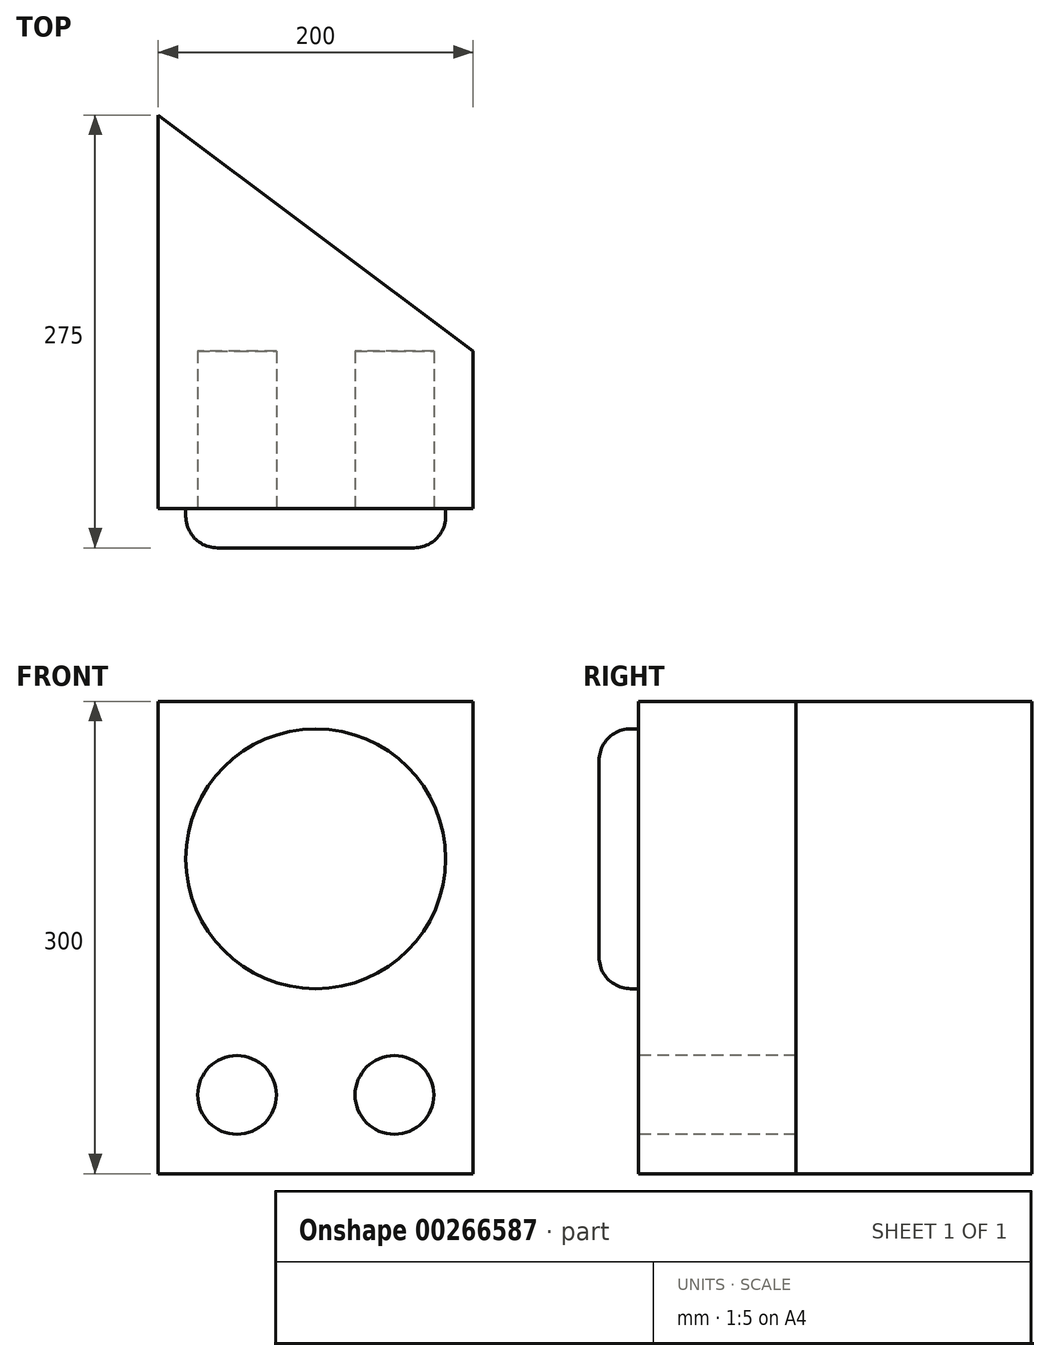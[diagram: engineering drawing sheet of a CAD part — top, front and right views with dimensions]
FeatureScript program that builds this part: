
annotation { "Feature Type Name" : "Feature", "Feature Type Description" : "" }
export const myFeature = defineFeature(function(context is Context, id is Id, definition is map)
    precondition{}
    {
        {
            var Q0;
            Q0=qCreatedBy(makeId("Front.planeOp"),FACE);
            var sketch = newSketch(context, id + "F0", { "sketchPlane" : qUnion([Q0])});
            skLineSegment(sketch, "E0.bottom", {"start": v(0, 0) * mm, "end": v(200, 0) * mm});
            skLineSegment(sketch, "E0.top", {"start": v(0, 300) * mm, "end": v(200, 300) * mm});
            skLineSegment(sketch, "E0.left", {"start": v(0, 0) * mm, "end": v(0, 300) * mm});
            skLineSegment(sketch, "E0.right", {"start": v(200, 0) * mm, "end": v(200, 300) * mm});
            skSolve(sketch);
        }
        {
            var Q0;
            Q0=makeQuery(id+"F0.imprint","IMPRINT",FACE,{"disambiguationData":[TD([[makeQuery(id+"F0.imprint","IMPRINT",EDGE,{"derivedFrom":sQuery(id+"F0.wireOp",EDGE,"E0.bottom")}),1.0]])]});
            extrude(context, id + "F1", {"entities" : qUnion([Q0]), "oppositeDirection" : true, "depth" : 250 * mm});
        }
        {
            var Q0;
            Q0=makeQuery(id+"F1.opExtrude","CAP_FACE",FACE,{"disambiguationData":[OSD([sQuery(id+"F0.wireOp",EDGE,"E0.bottom"),sQuery(id+"F0.wireOp",EDGE,"E0.top"),sQuery(id+"F0.wireOp",EDGE,"E0.left"),sQuery(id+"F0.wireOp",EDGE,"E0.right")])],"isStart":true});
            var sketch = newSketch(context, id + "F2", { "sketchPlane" : qUnion([Q0])});
            skCircle(sketch, "E1", {"center": v(100, 200) * mm, "radius": 82.5 * mm});
            skPoint(sketch, "E1.centerSnap0", {"position": v(100, 300) * mm});
            skSolve(sketch);
        }
        {
            var Q0;
            Q0=makeQuery(id+"F2.imprint","IMPRINT",FACE,{"disambiguationData":[TD([[makeQuery(id+"F2.imprint","IMPRINT",EDGE,{"derivedFrom":sQuery(id+"F2.wireOp",EDGE,"E1")}),1.0]])]});
            extrude(context, id + "F3", {"entities" : qUnion([Q0]), "operationType" : NewBodyOperationType.ADD, "depth" : 25 * mm});
        }
        {
            var Q0;
            Q0=makeQuery(id+"F1.opExtrude","SWEPT_FACE",FACE,{"disambiguationData":[OSD([sQuery(id+"F0.wireOp",EDGE,"E0.top")])]});
            var sketch = newSketch(context, id + "F4", { "sketchPlane" : qUnion([Q0])});
            skLineSegment(sketch, "E2", {"start": v(0, 250) * mm, "end": v(200, 100) * mm});
            skLineSegment(sketch, "E3", {"start": v(0, 250) * mm, "end": v(200, 250) * mm});
            skLineSegment(sketch, "E4", {"start": v(200, 250) * mm, "end": v(200, 100) * mm});
            skSolve(sketch);
        }
        {
            var Q0;
            Q0=makeQuery(id+"F4.imprint","IMPRINT",FACE,{"disambiguationData":[TD([[makeQuery(id+"F4.imprint","IMPRINT",EDGE,{"derivedFrom":sQuery(id+"F4.wireOp",EDGE,"E2")}),1.0]])]});
            extrude(context, id + "F5", {"entities" : qUnion([Q0]), "operationType" : NewBodyOperationType.REMOVE, "endBound" : BoundingType.THROUGH_ALL, "oppositeDirection" : true, "depth" : 25 * mm});
        }
        {
            var Q0;
            Q0=makeQuery(id+"F1.opExtrude","CAP_FACE",FACE,{"disambiguationData":[OSD([sQuery(id+"F0.wireOp",EDGE,"E0.bottom"),sQuery(id+"F0.wireOp",EDGE,"E0.top"),sQuery(id+"F0.wireOp",EDGE,"E0.left"),sQuery(id+"F0.wireOp",EDGE,"E0.right")])],"isStart":true});
            var sketch = newSketch(context, id + "F6", { "sketchPlane" : qUnion([Q0])});
            skCircle(sketch, "E5", {"center": v(150, 50) * mm, "radius": 25 * mm});
            skCircle(sketch, "E6", {"center": v(50, 50) * mm, "radius": 25 * mm});
            skSolve(sketch);
        }
        {
            var Q0;
            Q0 = qSketchRegion(id + "F6", true);
            extrude(context, id + "F7", {"entities" : qUnion([Q0]), "operationType" : NewBodyOperationType.REMOVE, "oppositeDirection" : true, "depth" : 100 * mm});
        }
        {
            var Q0;
            Q0=makeQuery(id+"F7.boolean.opBoolean","COPY",EDGE,{"derivedFrom":makeQuery(id+"F7.opExtrude","CAP_EDGE",EDGE,{"disambiguationData":[OSD([sQuery(id+"F6.wireOp",EDGE,"E6")])],"isStart":true})});
            var Q1;
            Q1=makeQuery(id+"F7.boolean.opBoolean","COPY",EDGE,{"derivedFrom":makeQuery(id+"F7.opExtrude","CAP_EDGE",EDGE,{"disambiguationData":[OSD([sQuery(id+"F6.wireOp",EDGE,"E5")])],"isStart":true})});
            var Q2;
            Q2=makeQuery(id+"F3.opExtrude","CAP_EDGE",EDGE,{"disambiguationData":[OSD([sQuery(id+"F2.wireOp",EDGE,"E1")])],"isStart":false});
            fillet(context, id + "F8", {"entities" : qUnion([Q0, Q1, Q2]), "radius" : 20 * mm, "tangentPropagation" : true, "allowEdgeOverflow" : false});
        }
    });
